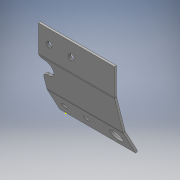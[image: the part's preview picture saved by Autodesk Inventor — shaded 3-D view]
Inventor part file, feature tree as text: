
AUTODESK INVENTOR PART (.ipt)
format: ipt  version: 2018 (Build 220112000, 112)  size: 281,600 bytes
history: native  units: mm
features: other x8, sketch x6, sheet_metal_op x3, hole x3, reference x2, plane x1, fillet x1, projected_geometry x1
ambient origin geometry x8: Origin, YZ Plane, XZ Plane, XY Plane, X Axis, Y Axis, Z Axis, Center Point
bodies: Body1 (feature_tree)
feature tree (25):
  other  "model.ipt"
  plane  "Work Plane1"
  sketch  "Sketch2"  dims[d7=10.0mm d9=5.0mm]
  sheet_metal_op  "Contour Flange1"
  hole  "Hole1"  [1 undecoded]
  hole  "Hole7"  [1 undecoded]
  hole  "Hole8"  [1 undecoded]
  sketch  "Sketch11"  dims[d16=5.0mm]
  fillet  "Fillet1"  Radius=180.0mm
  other  "Plate3"
  sheet_metal_op  "Bend2"
  sheet_metal_op  "Corner1"
  sketch  "Sketch8"  dims[d10=5.0mm d11=2.5mm]
  sketch  "Sketch9"  dims[d12=10.0mm d13=6.25mm d14=180.0mm]
  sketch  "Sketch10"  dims[d15=6.25mm]
  reference  "Reference1"
  reference  "Reference2"
  sketch  "Sketch12"  dims[d17=20.0mm d18=5.0mm d19=6.25mm d20=39.0mm d21=39.0mm d22=13.0mm d23=6.0mm d24=4.0mm d25=2.0mm d26=90.0deg d27=5.0mm d28=20.594885mm d74=62.052154mm d75=31.026077mm d76=26.0mm d77=52.0mm d78=81.718239mm d79=40.85912mm d80=26.0mm d81=52.0mm d82=13.0mm d83=6.0mm d84=4.0mm d85=2.0mm d86=90.0deg d87=5.0mm d88=20.594885mm d89=63.10912mm d90=31.55456mm d91=26.0mm d92=52.0mm d93=13.0mm d94=6.0mm d95=4.0mm d96=2.0mm d97=90.0deg d98=5.0mm d99=20.594885mm d100=20.0mm d101=20.0mm d102=302.737mm d103=30.0mm d104=302.737mm d105=5.0mm d106=0.0mm d107=18.5mm d108=30.0mm d109=62.052154mm d110=31.026077mm d111=31.026077mm d112=5.0mm d113=0.0mm d114=10.0mm d29=1.0mm d30=1.0mm]
  projected_geometry  "Projected Loop1"
  other  "Cut1"
  other  "Cut2"
  parser-record x1  (decoder bookkeeping rows leaked as tree rows — omitted from the tree; the rows remain in map.json)
  other  "modul.iam"
  other  "vange:1"
  other  "Definition1"
note: 3 required parameter values undecoded (feature->parameter linkage not recoverable at this tier; creation-order binding heuristic only, values carry confidence <= 0.55)
note: 1 file-system path scrubbed to <path> (originals preserved in map.json)
